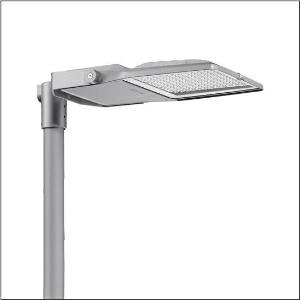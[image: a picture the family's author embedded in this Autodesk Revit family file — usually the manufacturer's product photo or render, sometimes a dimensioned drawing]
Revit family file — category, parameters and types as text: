
# Revit family: floodlight_fl_21_midi___pl33t_5xa7786e2f3a_2de9
name_source: partatom
category: Lighting Fixtures
units: mm (PartAtom-declared; Revit-internal decimal feet)

## family parameters
Cut with Voids When Loaded = No
Host = Face
Light Source = No
Part Type = Normal
Room Calculation Point = No
Round Connector Dimension = Use Diameter
Shared = No

## types (1)
- --- (1 x LED, 26630 lm, 212.4 W, 3000K)
    Apparent Load = 212 VA
    CIE Flux Codes = 26 75 99 100 100
    Color Rendering = 70
    Color Temperature = 3000K
    Default Elevation = 1800 mm
    Description = Floodlight FL 21 midi, floodlight, primary light control with lens, of PMMA, primary optical cover: protective disc, of toughened safety glass, transparent, light distribution: PL33T, light emission: direct distribution, installation type: surface-mounted, LED, High Power LED, rated luminous flux: 26.630lm, luminous efficacy: 125lm/W, light colour: 730, colour temperature: 3000K, control gear: ECG Smart Interface, control: flexible luminous flux parameterisation, time-dependent luminous flux control, constant luminous flux control, overheat protection, presetting dimming logarithmic, with terminal, 6-pole, mains connection: 220..240V, AC, 50/60Hz, start of lifetime: 212W, end of service life: 231W, reduction: 95W, luminaire housing, of diecast aluminium, powder-coated, Siteco® metallic grey (DB 702S), corrosivity category C5 mid according to DIN EN ISO 12944, sealing non-destructively replaceable, please order mast flange separately, mast bracket, of steel, galvanised, powder-coated, Siteco® metallic grey (DB 702S), Smart Interface below and above, protection rating (complete): IP66, insulation class (complete): insulation class II (safety insulation), certification: CE, protection symbol: D, impact resistance: IK08, permissible operating ambient temperature: -40..+40°C, permissible operating ambient temperature for outdoor applications: -40..+50°C, standard: DIN EN 12944, LABS conformity tested according to VDMA 24364:2018-05, packaging unit: 1 piece

Light Distribution: PL33T
    Height = 76 mm
    Lamp = 1 x LED
    Lamp Light Flux = 26630 lm
    Lamp Power = 212.4 W
    Lamp count = 1
    Length = 657 mm
    Luminous efficacy = 125 lm/W
    Manufacturer = Siteco
    ModVariant = No
    Model = 5XA7786E2F3A
    Number of Poles = 1
    OnlyDefault = Yes
    Power Factor = 1
    Product Name = Floodlight FL 21 midi | PL33T
    Product group = floodlight | pylon annexe
    ProductGroupID = 6200
    Protection Class = Protection class II
    Protection Degree = IP 66
    RLX_Detail_Level = 1
    RLX_Emergency_Light_Flux = 0 lm
    RLX_Emergency_Type = 0
    RLX_Emergency_Type_DB = No
    RlxData = <blob elided: 153505 chars, md5=c08c4b49>
    Socket = socket
    Standby Power = 0 W
    System Light Flux = 26630 lm
    System Power = 212 W
    Type Comments = factory setting: luminous flux: 100 % | dim-lin: 254 | 710 mA
    Type Image = l_1007123.jpg
    URL = http://relux.com
    VarID = @adj_100701
    Voltage = 0 V
    Weight = 0.00 kg
    Width = 442 mm

## geometry (parser evidence)
native form markers: Blend x4, Sweep x13
no freeform markers — native parametric forms only
